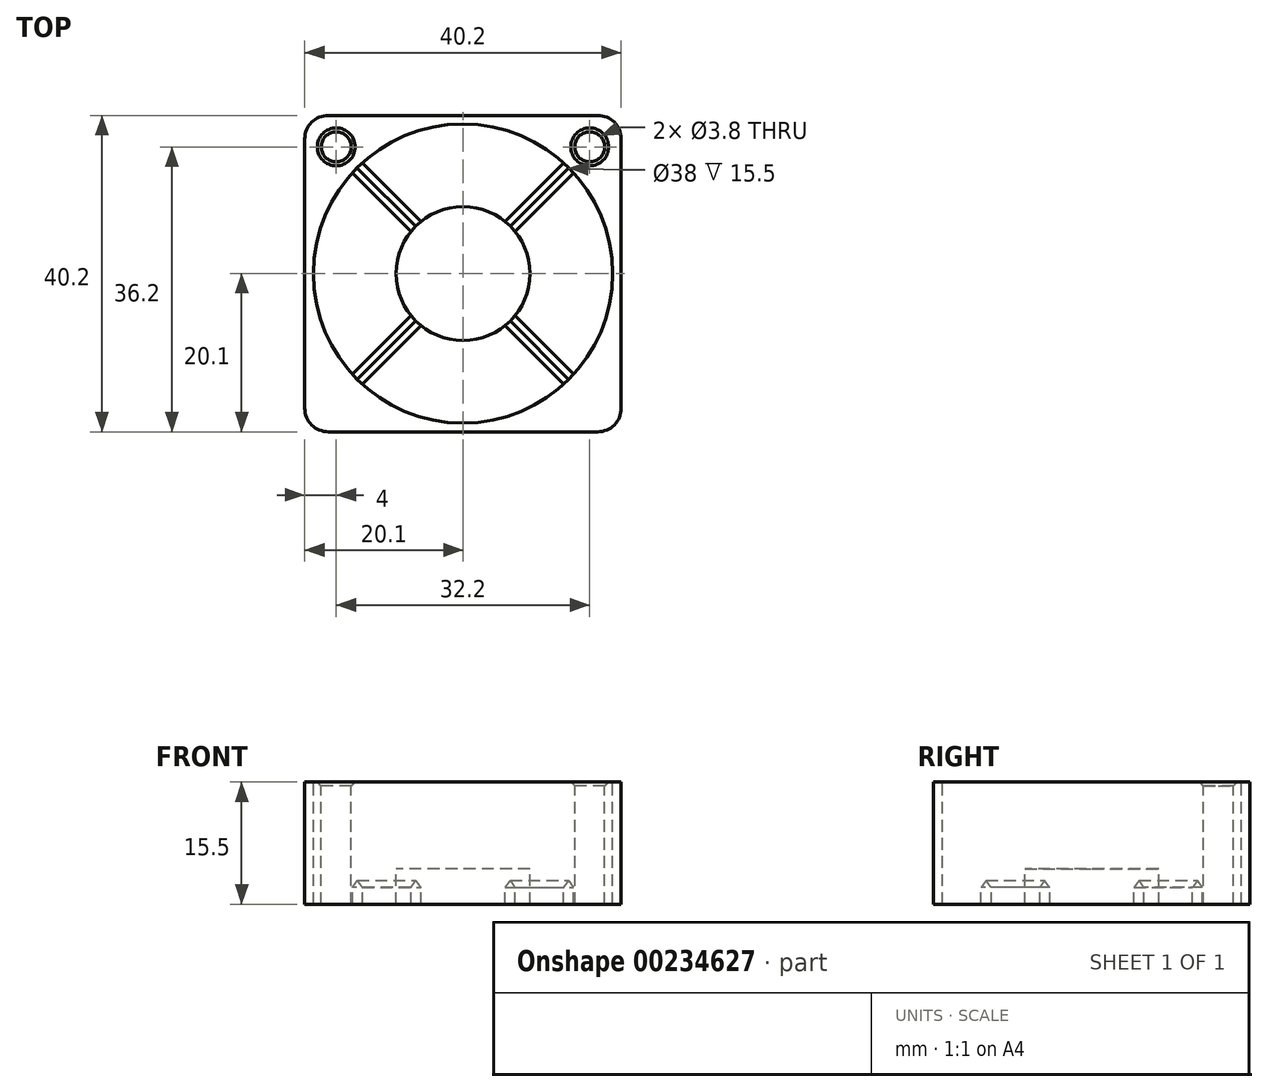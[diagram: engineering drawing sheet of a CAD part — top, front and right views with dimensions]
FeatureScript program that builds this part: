
annotation { "Feature Type Name" : "Feature", "Feature Type Description" : "" }
export const myFeature = defineFeature(function(context is Context, id is Id, definition is map)
    precondition{}
    {
        {
            var Q0;
            Q0=qCreatedBy(makeId("Top.planeOp"),FACE);
            var sketch = newSketch(context, id + "F0", { "sketchPlane" : qUnion([Q0])});
            skLineSegment(sketch, "E0.bottom", {"start": v(17.1, -20.1) * mm, "end": v(-17.1, -20.1) * mm});
            skLineSegment(sketch, "E0.top", {"start": v(17.1, 20.1) * mm, "end": v(-17.1, 20.1) * mm});
            skLineSegment(sketch, "E0.left", {"start": v(20.1, -17.1) * mm, "end": v(20.1, 17.1) * mm});
            skLineSegment(sketch, "E0.right", {"start": v(-20.1, -17.1) * mm, "end": v(-20.1, 17.1) * mm});
            skPoint(sketch, "E0.middle", {"position": v(0, 0) * mm});
            skPoint(sketch, "E1.visualSharp", {"position": v(-20.1, 20.1) * mm});
            skArc(sketch, "E1.filletArc", {"start": v(-17.1, 20.1) * mm, "mid": v(-19.22, 19.22) * mm, "end": v(-20.1, 17.1) * mm});
            skPoint(sketch, "E2.visualSharp", {"position": v(20.1, 20.1) * mm});
            skArc(sketch, "E2.filletArc", {"start": v(20.1, 17.1) * mm, "mid": v(19.22, 19.22) * mm, "end": v(17.1, 20.1) * mm});
            skPoint(sketch, "E3.visualSharp", {"position": v(20.1, -20.1) * mm});
            skArc(sketch, "E3.filletArc", {"start": v(17.1, -20.1) * mm, "mid": v(19.22, -19.22) * mm, "end": v(20.1, -17.1) * mm});
            skPoint(sketch, "E4.visualSharp", {"position": v(-20.1, -20.1) * mm});
            skArc(sketch, "E4.filletArc", {"start": v(-20.1, -17.1) * mm, "mid": v(-19.22, -19.22) * mm, "end": v(-17.1, -20.1) * mm});
            skCircle(sketch, "E5", {"center": v(0, 0) * mm, "radius": 19 * mm});
            skCircle(sketch, "E6", {"center": v(0, 0) * mm, "radius": 8.5 * mm});
            skLineSegment(sketch, "E7", {"start": v(-17.1, -17.1) * mm, "end": v(17.1, 17.1) * mm, "construction": true});
            skLineSegment(sketch, "E8", {"start": v(-17.1, 17.1) * mm, "end": v(17.1, -17.1) * mm, "construction": true});
            skLineSegment(sketch, "E9", {"start": v(-14.06, -12.78) * mm, "end": v(-6.61, -5.34) * mm});
            skLineSegment(sketch, "E10", {"start": v(-5.34, -6.61) * mm, "end": v(-12.78, -14.06) * mm});
            skLineSegment(sketch, "E11", {"start": v(12.78, -14.06) * mm, "end": v(5.34, -6.61) * mm});
            skLineSegment(sketch, "E12", {"start": v(6.61, -5.34) * mm, "end": v(14.06, -12.78) * mm});
            skLineSegment(sketch, "E13.MirrorCS", {"start": v(6.61, 5.34) * mm, "end": v(14.06, 12.78) * mm});
            skLineSegment(sketch, "E14.MirrorCS", {"start": v(12.78, 14.06) * mm, "end": v(5.34, 6.61) * mm});
            skLineSegment(sketch, "E15.MirrorCS", {"start": v(-5.34, 6.61) * mm, "end": v(-12.78, 14.06) * mm});
            skLineSegment(sketch, "E16.MirrorCS", {"start": v(-14.06, 12.78) * mm, "end": v(-6.61, 5.34) * mm});
            skCircle(sketch, "E17", {"center": v(-16.1, -16.1) * mm, "radius": 1.9 * mm});
            skCircle(sketch, "E18", {"center": v(16.1, -16.1) * mm, "radius": 1.9 * mm});
            skCircle(sketch, "E19.MirrorC", {"center": v(16.1, 16.1) * mm, "radius": 1.9 * mm});
            skCircle(sketch, "E20.MirrorC", {"center": v(-16.1, 16.1) * mm, "radius": 1.9 * mm});
            skLineSegment(sketch, "E21", {"start": v(20.1, 0) * mm, "end": v(-20.1, 0) * mm, "construction": true});
            skSolve(sketch);
        }
        {
            var Q0;
            Q0=makeQuery(id+"F0.imprint","IMPRINT",FACE,{"disambiguationData":[TD([[makeQuery(id+"F0.imprint","IMPRINT",EDGE,{"derivedFrom":sQuery(id+"F0.wireOp",EDGE,"E0.bottom")}),-1.0]])]});
            var Q1;
            {var subQ0=sQuery(id+"F0.wireOp",EDGE,"E15.MirrorCS");var subQ1=sQuery(id+"F0.wireOp",EDGE,"E5");var subQ2=makeQuery(id+"F0.imprint","INTERSECT",VERTEX,{"derivedFrom":[subQ1,subQ0]});Q1=makeQuery(id+"F0.imprint","IMPRINT",FACE,{"disambiguationData":[TD([[makeQuery(id+"F0.imprint","IMPRINT",EDGE,{"disambiguationData":[TD([[subQ2,-1.0]])],"derivedFrom":subQ1}),1.0]])]});}
            var Q2;
            {var subQ0=sQuery(id+"F0.wireOp",EDGE,"E15.MirrorCS");var subQ1=sQuery(id+"F0.wireOp",EDGE,"E6");var subQ2=makeQuery(id+"F0.imprint","INTERSECT",VERTEX,{"derivedFrom":[subQ1,subQ0]});Q2=makeQuery(id+"F0.imprint","IMPRINT",FACE,{"disambiguationData":[TD([[makeQuery(id+"F0.imprint","IMPRINT",EDGE,{"disambiguationData":[TD([[subQ2,-1.0]])],"derivedFrom":subQ1}),-1.0]])]});}
            var Q3;
            {var subQ0=sQuery(id+"F0.wireOp",EDGE,"OKVz19BP-hNnI-5fpd-Gdqc-Ac2bVMNZXSYf");var subQ1=sQuery(id+"F0.wireOp",EDGE,"E15.MirrorCS");var subQ2=makeQuery(id+"F0.imprint","INTERSECT",VERTEX,{"derivedFrom":[subQ1,subQ0]});Q3=makeQuery(id+"F0.imprint","IMPRINT",FACE,{"disambiguationData":[TD([[makeQuery(id+"F0.imprint","IMPRINT",EDGE,{"disambiguationData":[TD([[subQ2,-1.0]])],"derivedFrom":subQ1}),1.0]])]});}
            var Q4;
            {var subQ0=sQuery(id+"F0.wireOp",EDGE,"E13.MirrorCS");var subQ1=sQuery(id+"F0.wireOp",EDGE,"E5");var subQ2=makeQuery(id+"F0.imprint","INTERSECT",VERTEX,{"derivedFrom":[subQ1,subQ0]});Q4=makeQuery(id+"F0.imprint","IMPRINT",FACE,{"disambiguationData":[TD([[makeQuery(id+"F0.imprint","IMPRINT",EDGE,{"disambiguationData":[TD([[subQ2,-1.0]])],"derivedFrom":subQ1}),1.0]])]});}
            var Q5;
            {var subQ0=sQuery(id+"F0.wireOp",EDGE,"OKVz19BP-hNnI-5fpd-Gdqc-Ac2bVMNZXSYf");var subQ1=sQuery(id+"F0.wireOp",EDGE,"E13.MirrorCS");var subQ2=makeQuery(id+"F0.imprint","INTERSECT",VERTEX,{"derivedFrom":[subQ1,subQ0]});Q5=makeQuery(id+"F0.imprint","IMPRINT",FACE,{"disambiguationData":[TD([[makeQuery(id+"F0.imprint","IMPRINT",EDGE,{"disambiguationData":[TD([[subQ2,-1.0]])],"derivedFrom":subQ1}),1.0]])]});}
            var Q6;
            {var subQ0=sQuery(id+"F0.wireOp",EDGE,"E13.MirrorCS");var subQ1=sQuery(id+"F0.wireOp",EDGE,"E6");var subQ2=makeQuery(id+"F0.imprint","INTERSECT",VERTEX,{"derivedFrom":[subQ1,subQ0]});Q6=makeQuery(id+"F0.imprint","IMPRINT",FACE,{"disambiguationData":[TD([[makeQuery(id+"F0.imprint","IMPRINT",EDGE,{"disambiguationData":[TD([[subQ2,-1.0]])],"derivedFrom":subQ1}),-1.0]])]});}
            var Q7;
            {var subQ0=sQuery(id+"F0.wireOp",EDGE,"E6");var subQ5=makeQuery(id+"F0.imprint","INTERSECT",VERTEX,{"derivedFrom":[subQ0,sQuery(id+"F0.wireOp",EDGE,"E13.MirrorCS")]});Q7=makeQuery(id+"F0.imprint","IMPRINT",FACE,{"disambiguationData":[TD([[makeQuery(id+"F0.imprint","IMPRINT",EDGE,{"disambiguationData":[TD([[subQ5,-1.0]])],"derivedFrom":subQ0}),1.0]])]});}
            var Q8;
            {var subQ0=sQuery(id+"F0.wireOp",EDGE,"E11");var subQ1=sQuery(id+"F0.wireOp",EDGE,"E6");var subQ2=makeQuery(id+"F0.imprint","INTERSECT",VERTEX,{"derivedFrom":[subQ1,subQ0]});Q8=makeQuery(id+"F0.imprint","IMPRINT",FACE,{"disambiguationData":[TD([[makeQuery(id+"F0.imprint","IMPRINT",EDGE,{"disambiguationData":[TD([[subQ2,-1.0]])],"derivedFrom":subQ1}),-1.0]])]});}
            var Q9;
            {var subQ0=sQuery(id+"F0.wireOp",EDGE,"1LaAh6nE-W3w1-AZA4-EiVi-7yOxxJTW6hyr");var subQ1=sQuery(id+"F0.wireOp",EDGE,"E11");var subQ2=makeQuery(id+"F0.imprint","INTERSECT",VERTEX,{"derivedFrom":[subQ1,subQ0]});Q9=makeQuery(id+"F0.imprint","IMPRINT",FACE,{"disambiguationData":[TD([[makeQuery(id+"F0.imprint","IMPRINT",EDGE,{"disambiguationData":[TD([[subQ2,-1.0]])],"derivedFrom":subQ1}),-1.0]])]});}
            var Q10;
            {var subQ0=sQuery(id+"F0.wireOp",EDGE,"E11");var subQ1=sQuery(id+"F0.wireOp",EDGE,"E5");var subQ2=makeQuery(id+"F0.imprint","INTERSECT",VERTEX,{"derivedFrom":[subQ1,subQ0]});Q10=makeQuery(id+"F0.imprint","IMPRINT",FACE,{"disambiguationData":[TD([[makeQuery(id+"F0.imprint","IMPRINT",EDGE,{"disambiguationData":[TD([[subQ2,-1.0]])],"derivedFrom":subQ1}),1.0]])]});}
            var Q11;
            {var subQ0=sQuery(id+"F0.wireOp",EDGE,"1LaAh6nE-W3w1-AZA4-EiVi-7yOxxJTW6hyr");var subQ1=sQuery(id+"F0.wireOp",EDGE,"E9");var subQ2=makeQuery(id+"F0.imprint","INTERSECT",VERTEX,{"derivedFrom":[subQ1,subQ0]});Q11=makeQuery(id+"F0.imprint","IMPRINT",FACE,{"disambiguationData":[TD([[makeQuery(id+"F0.imprint","IMPRINT",EDGE,{"disambiguationData":[TD([[subQ2,-1.0]])],"derivedFrom":subQ1}),-1.0]])]});}
            var Q12;
            {var subQ0=sQuery(id+"F0.wireOp",EDGE,"E9");var subQ1=sQuery(id+"F0.wireOp",EDGE,"E6");var subQ2=makeQuery(id+"F0.imprint","INTERSECT",VERTEX,{"derivedFrom":[subQ1,subQ0]});Q12=makeQuery(id+"F0.imprint","IMPRINT",FACE,{"disambiguationData":[TD([[makeQuery(id+"F0.imprint","IMPRINT",EDGE,{"disambiguationData":[TD([[subQ2,-1.0]])],"derivedFrom":subQ1}),-1.0]])]});}
            var Q13;
            {var subQ0=sQuery(id+"F0.wireOp",EDGE,"E9");var subQ1=sQuery(id+"F0.wireOp",EDGE,"E5");var subQ2=makeQuery(id+"F0.imprint","INTERSECT",VERTEX,{"derivedFrom":[subQ1,subQ0]});Q13=makeQuery(id+"F0.imprint","IMPRINT",FACE,{"disambiguationData":[TD([[makeQuery(id+"F0.imprint","IMPRINT",EDGE,{"disambiguationData":[TD([[subQ2,-1.0]])],"derivedFrom":subQ1}),1.0]])]});}
            var Q14;
            Q14=makeQuery(id+"F0.imprint","IMPRINT",FACE,{"disambiguationData":[TD([[makeQuery(id+"F0.imprint","IMPRINT",EDGE,{"derivedFrom":sQuery(id+"F0.wireOp",EDGE,"E17")}),1.0]])]});
            var Q15;
            Q15=makeQuery(id+"F0.imprint","IMPRINT",FACE,{"disambiguationData":[TD([[makeQuery(id+"F0.imprint","IMPRINT",EDGE,{"derivedFrom":sQuery(id+"F0.wireOp",EDGE,"E18")}),1.0]])]});
            var Q16;
            Q16=makeQuery(id+"F0.imprint","IMPRINT",FACE,{"disambiguationData":[TD([[makeQuery(id+"F0.imprint","IMPRINT",EDGE,{"derivedFrom":sQuery(id+"F0.wireOp",EDGE,"E20.MirrorC")}),-1.0]])]});
            var Q17;
            Q17=makeQuery(id+"F0.imprint","IMPRINT",FACE,{"disambiguationData":[TD([[makeQuery(id+"F0.imprint","IMPRINT",EDGE,{"derivedFrom":sQuery(id+"F0.wireOp",EDGE,"E19.MirrorC")}),-1.0]])]});
            extrude(context, id + "F1", {"entities" : qUnion([Q0, Q1, Q2, Q3, Q4, Q5, Q6, Q7, Q8, Q9, Q10, Q11, Q12, Q13, Q14, Q15, Q16, Q17]), "oppositeDirection" : true, "depth" : 3 * mm});
        }
        {
            var Q0;
            Q0=makeQuery(id+"F0.imprint","IMPRINT",FACE,{"disambiguationData":[TD([[makeQuery(id+"F0.imprint","IMPRINT",EDGE,{"derivedFrom":sQuery(id+"F0.wireOp",EDGE,"E0.bottom")}),-1.0]])]});
            var Q1;
            {var subQ0=sQuery(id+"F0.wireOp",EDGE,"E6");var subQ5=makeQuery(id+"F0.imprint","INTERSECT",VERTEX,{"derivedFrom":[subQ0,sQuery(id+"F0.wireOp",EDGE,"E13.MirrorCS")]});Q1=makeQuery(id+"F0.imprint","IMPRINT",FACE,{"disambiguationData":[TD([[makeQuery(id+"F0.imprint","IMPRINT",EDGE,{"disambiguationData":[TD([[subQ5,-1.0]])],"derivedFrom":subQ0}),1.0]])]});}
            var Q2;
            Q2=makeQuery(id+"F0.imprint","IMPRINT",FACE,{"disambiguationData":[TD([[makeQuery(id+"F0.imprint","IMPRINT",EDGE,{"derivedFrom":sQuery(id+"F0.wireOp",EDGE,"E17")}),1.0]])]});
            var Q3;
            Q3=makeQuery(id+"F0.imprint","IMPRINT",FACE,{"disambiguationData":[TD([[makeQuery(id+"F0.imprint","IMPRINT",EDGE,{"derivedFrom":sQuery(id+"F0.wireOp",EDGE,"E18")}),1.0]])]});
            var Q4;
            Q4=makeQuery(id+"F0.imprint","IMPRINT",FACE,{"disambiguationData":[TD([[makeQuery(id+"F0.imprint","IMPRINT",EDGE,{"derivedFrom":sQuery(id+"F0.wireOp",EDGE,"E19.MirrorC")}),-1.0]])]});
            var Q5;
            Q5=makeQuery(id+"F0.imprint","IMPRINT",FACE,{"disambiguationData":[TD([[makeQuery(id+"F0.imprint","IMPRINT",EDGE,{"derivedFrom":sQuery(id+"F0.wireOp",EDGE,"E20.MirrorC")}),-1.0]])]});
            extrude(context, id + "F2", {"entities" : qUnion([Q0, Q1, Q2, Q3, Q4, Q5]), "operationType" : NewBodyOperationType.ADD, "depth" : 1.5 * mm});
        }
        {
            var Q0;
            Q0=makeQuery(id+"F0.imprint","IMPRINT",FACE,{"disambiguationData":[TD([[makeQuery(id+"F0.imprint","IMPRINT",EDGE,{"derivedFrom":sQuery(id+"F0.wireOp",EDGE,"E17")}),1.0]])]});
            var Q1;
            Q1=makeQuery(id+"F0.imprint","IMPRINT",FACE,{"disambiguationData":[TD([[makeQuery(id+"F0.imprint","IMPRINT",EDGE,{"derivedFrom":sQuery(id+"F0.wireOp",EDGE,"E18")}),1.0]])]});
            var Q2;
            Q2=makeQuery(id+"F0.imprint","IMPRINT",FACE,{"disambiguationData":[TD([[makeQuery(id+"F0.imprint","IMPRINT",EDGE,{"derivedFrom":sQuery(id+"F0.wireOp",EDGE,"E19.MirrorC")}),-1.0]])]});
            var Q3;
            Q3=makeQuery(id+"F0.imprint","IMPRINT",FACE,{"disambiguationData":[TD([[makeQuery(id+"F0.imprint","IMPRINT",EDGE,{"derivedFrom":sQuery(id+"F0.wireOp",EDGE,"E20.MirrorC")}),-1.0]])]});
            extrude(context, id + "F3", {"entities" : qUnion([Q0, Q1, Q2, Q3]), "operationType" : NewBodyOperationType.ADD, "depth" : 12.5 * mm});
        }
        {
            var Q0;
            Q0=makeQuery(id+"F2.opExtrude","CAP_EDGE",EDGE,{"disambiguationData":[OSD([sQuery(id+"F0.wireOp",EDGE,"E5")])],"isStart":false});
            var Q1;
            Q1=makeQuery(id+"F3.opExtrude","CAP_EDGE",EDGE,{"disambiguationData":[OSD([sQuery(id+"F0.wireOp",EDGE,"E18")])],"isStart":false});
            var Q2;
            Q2=makeQuery(id+"F3.opExtrude","CAP_EDGE",EDGE,{"disambiguationData":[OSD([sQuery(id+"F0.wireOp",EDGE,"E17")])],"isStart":false});
            var Q3;
            Q3=makeQuery(id+"F3.opExtrude","CAP_EDGE",EDGE,{"disambiguationData":[OSD([sQuery(id+"F0.wireOp",EDGE,"E20.MirrorC")])],"isStart":false});
            var Q4;
            Q4=makeQuery(id+"F3.opExtrude","CAP_EDGE",EDGE,{"disambiguationData":[OSD([sQuery(id+"F0.wireOp",EDGE,"E19.MirrorC")])],"isStart":false});
            chamfer(context, id + "F4", {"entities" : qUnion([Q0, Q1, Q2, Q3, Q4]), "width" : 0.5 * mm, "tangentPropagation" : true});
        }
        {
            var Q0;
            {var subQ0=sQuery(id+"F0.wireOp",EDGE,"OKVz19BP-hNnI-5fpd-Gdqc-Ac2bVMNZXSYf");Q0=makeQuery(id+"F1.opExtrude","CAP_EDGE",EDGE,{"disambiguationData":[OSD([subQ0]),TDD([makeQuery(id+"F0.imprint","IMPRINT",EDGE,{"disambiguationData":[TD([[makeQuery(id+"F0.imprint","INTERSECT",VERTEX,{"derivedFrom":[sQuery(id+"F0.wireOp",EDGE,"E10"),subQ0]}),-1.0]])],"derivedFrom":subQ0})])],"isStart":true});}
            var Q1;
            {var subQ0=sQuery(id+"F0.wireOp",EDGE,"1LaAh6nE-W3w1-AZA4-EiVi-7yOxxJTW6hyr");Q1=makeQuery(id+"F1.opExtrude","CAP_EDGE",EDGE,{"disambiguationData":[OSD([subQ0]),TDD([makeQuery(id+"F0.imprint","IMPRINT",EDGE,{"disambiguationData":[TD([[makeQuery(id+"F0.imprint","INTERSECT",VERTEX,{"derivedFrom":[sQuery(id+"F0.wireOp",EDGE,"E10"),subQ0]}),-1.0]])],"derivedFrom":subQ0})])],"isStart":true});}
            var Q2;
            {var subQ0=sQuery(id+"F0.wireOp",EDGE,"E11");Q2=makeQuery(id+"F1.opExtrude","CAP_EDGE",EDGE,{"disambiguationData":[OSD([subQ0]),TDD([makeQuery(id+"F0.imprint","IMPRINT",EDGE,{"disambiguationData":[TD([[makeQuery(id+"F0.imprint","INTERSECT",VERTEX,{"derivedFrom":[sQuery(id+"F0.wireOp",EDGE,"E5"),subQ0]}),-1.0]])],"derivedFrom":subQ0})])],"isStart":true});}
            var Q3;
            {var subQ0=sQuery(id+"F0.wireOp",EDGE,"E12");Q3=makeQuery(id+"F1.opExtrude","CAP_EDGE",EDGE,{"disambiguationData":[OSD([subQ0]),TDD([makeQuery(id+"F0.imprint","IMPRINT",EDGE,{"disambiguationData":[TD([[makeQuery(id+"F0.imprint","INTERSECT",VERTEX,{"derivedFrom":[sQuery(id+"F0.wireOp",EDGE,"E5"),subQ0]}),1.0]])],"derivedFrom":subQ0})])],"isStart":true});}
            var Q4;
            {var subQ0=sQuery(id+"F0.wireOp",EDGE,"E11");Q4=makeQuery(id+"F1.opExtrude","CAP_EDGE",EDGE,{"disambiguationData":[OSD([subQ0]),TDD([makeQuery(id+"F0.imprint","IMPRINT",EDGE,{"disambiguationData":[TD([[makeQuery(id+"F0.imprint","INTERSECT",VERTEX,{"derivedFrom":[sQuery(id+"F0.wireOp",EDGE,"E6"),subQ0]}),1.0]])],"derivedFrom":subQ0})])],"isStart":true});}
            var Q5;
            {var subQ0=sQuery(id+"F0.wireOp",EDGE,"E12");Q5=makeQuery(id+"F1.opExtrude","CAP_EDGE",EDGE,{"disambiguationData":[OSD([subQ0]),TDD([makeQuery(id+"F0.imprint","IMPRINT",EDGE,{"disambiguationData":[TD([[makeQuery(id+"F0.imprint","INTERSECT",VERTEX,{"derivedFrom":[sQuery(id+"F0.wireOp",EDGE,"E6"),subQ0]}),-1.0]])],"derivedFrom":subQ0})])],"isStart":true});}
            var Q6;
            {var subQ0=sQuery(id+"F0.wireOp",EDGE,"OKVz19BP-hNnI-5fpd-Gdqc-Ac2bVMNZXSYf");Q6=makeQuery(id+"F1.opExtrude","CAP_EDGE",EDGE,{"disambiguationData":[OSD([subQ0]),TDD([makeQuery(id+"F0.imprint","IMPRINT",EDGE,{"disambiguationData":[TD([[makeQuery(id+"F0.imprint","INTERSECT",VERTEX,{"derivedFrom":[sQuery(id+"F0.wireOp",EDGE,"E12"),subQ0]}),-1.0]])],"derivedFrom":subQ0})])],"isStart":true});}
            var Q7;
            {var subQ0=sQuery(id+"F0.wireOp",EDGE,"1LaAh6nE-W3w1-AZA4-EiVi-7yOxxJTW6hyr");Q7=makeQuery(id+"F1.opExtrude","CAP_EDGE",EDGE,{"disambiguationData":[OSD([subQ0]),TDD([makeQuery(id+"F0.imprint","IMPRINT",EDGE,{"disambiguationData":[TD([[makeQuery(id+"F0.imprint","INTERSECT",VERTEX,{"derivedFrom":[sQuery(id+"F0.wireOp",EDGE,"E12"),subQ0]}),-1.0]])],"derivedFrom":subQ0})])],"isStart":true});}
            var Q8;
            {var subQ0=sQuery(id+"F0.wireOp",EDGE,"E10");Q8=makeQuery(id+"F1.opExtrude","CAP_EDGE",EDGE,{"disambiguationData":[OSD([subQ0]),TDD([makeQuery(id+"F0.imprint","IMPRINT",EDGE,{"disambiguationData":[TD([[makeQuery(id+"F0.imprint","INTERSECT",VERTEX,{"derivedFrom":[sQuery(id+"F0.wireOp",EDGE,"E5"),subQ0]}),1.0]])],"derivedFrom":subQ0})])],"isStart":true});}
            var Q9;
            {var subQ0=sQuery(id+"F0.wireOp",EDGE,"E9");Q9=makeQuery(id+"F1.opExtrude","CAP_EDGE",EDGE,{"disambiguationData":[OSD([subQ0]),TDD([makeQuery(id+"F0.imprint","IMPRINT",EDGE,{"disambiguationData":[TD([[makeQuery(id+"F0.imprint","INTERSECT",VERTEX,{"derivedFrom":[sQuery(id+"F0.wireOp",EDGE,"E5"),subQ0]}),-1.0]])],"derivedFrom":subQ0})])],"isStart":true});}
            var Q10;
            {var subQ0=sQuery(id+"F0.wireOp",EDGE,"1LaAh6nE-W3w1-AZA4-EiVi-7yOxxJTW6hyr");Q10=makeQuery(id+"F1.opExtrude","CAP_EDGE",EDGE,{"disambiguationData":[OSD([subQ0]),TDD([makeQuery(id+"F0.imprint","IMPRINT",EDGE,{"disambiguationData":[TD([[makeQuery(id+"F0.imprint","INTERSECT",VERTEX,{"derivedFrom":[sQuery(id+"F0.wireOp",EDGE,"E9"),subQ0]}),1.0]])],"derivedFrom":subQ0})])],"isStart":true});}
            var Q11;
            {var subQ0=sQuery(id+"F0.wireOp",EDGE,"OKVz19BP-hNnI-5fpd-Gdqc-Ac2bVMNZXSYf");Q11=makeQuery(id+"F1.opExtrude","CAP_EDGE",EDGE,{"disambiguationData":[OSD([subQ0]),TDD([makeQuery(id+"F0.imprint","IMPRINT",EDGE,{"disambiguationData":[TD([[makeQuery(id+"F0.imprint","INTERSECT",VERTEX,{"derivedFrom":[sQuery(id+"F0.wireOp",EDGE,"E9"),subQ0]}),1.0]])],"derivedFrom":subQ0})])],"isStart":true});}
            var Q12;
            {var subQ0=sQuery(id+"F0.wireOp",EDGE,"E9");Q12=makeQuery(id+"F1.opExtrude","CAP_EDGE",EDGE,{"disambiguationData":[OSD([subQ0]),TDD([makeQuery(id+"F0.imprint","IMPRINT",EDGE,{"disambiguationData":[TD([[makeQuery(id+"F0.imprint","INTERSECT",VERTEX,{"derivedFrom":[sQuery(id+"F0.wireOp",EDGE,"E6"),subQ0]}),1.0]])],"derivedFrom":subQ0})])],"isStart":true});}
            var Q13;
            {var subQ0=sQuery(id+"F0.wireOp",EDGE,"E10");Q13=makeQuery(id+"F1.opExtrude","CAP_EDGE",EDGE,{"disambiguationData":[OSD([subQ0]),TDD([makeQuery(id+"F0.imprint","IMPRINT",EDGE,{"disambiguationData":[TD([[makeQuery(id+"F0.imprint","INTERSECT",VERTEX,{"derivedFrom":[sQuery(id+"F0.wireOp",EDGE,"E6"),subQ0]}),-1.0]])],"derivedFrom":subQ0})])],"isStart":true});}
            var Q14;
            {var subQ0=sQuery(id+"F0.wireOp",EDGE,"E16.MirrorCS");Q14=makeQuery(id+"F1.opExtrude","CAP_EDGE",EDGE,{"disambiguationData":[OSD([subQ0]),TDD([makeQuery(id+"F0.imprint","IMPRINT",EDGE,{"disambiguationData":[TD([[makeQuery(id+"F0.imprint","INTERSECT",VERTEX,{"derivedFrom":[sQuery(id+"F0.wireOp",EDGE,"E6"),subQ0]}),1.0]])],"derivedFrom":subQ0})])],"isStart":true});}
            var Q15;
            {var subQ0=sQuery(id+"F0.wireOp",EDGE,"E15.MirrorCS");Q15=makeQuery(id+"F1.opExtrude","CAP_EDGE",EDGE,{"disambiguationData":[OSD([subQ0]),TDD([makeQuery(id+"F0.imprint","IMPRINT",EDGE,{"disambiguationData":[TD([[makeQuery(id+"F0.imprint","INTERSECT",VERTEX,{"derivedFrom":[sQuery(id+"F0.wireOp",EDGE,"E6"),subQ0]}),-1.0]])],"derivedFrom":subQ0})])],"isStart":true});}
            var Q16;
            {var subQ0=sQuery(id+"F0.wireOp",EDGE,"OKVz19BP-hNnI-5fpd-Gdqc-Ac2bVMNZXSYf");Q16=makeQuery(id+"F1.opExtrude","CAP_EDGE",EDGE,{"disambiguationData":[OSD([subQ0]),TDD([makeQuery(id+"F0.imprint","IMPRINT",EDGE,{"disambiguationData":[TD([[makeQuery(id+"F0.imprint","INTERSECT",VERTEX,{"derivedFrom":[sQuery(id+"F0.wireOp",EDGE,"E14.MirrorCS"),subQ0]}),-1.0]])],"derivedFrom":subQ0})])],"isStart":true});}
            var Q17;
            {var subQ0=sQuery(id+"F0.wireOp",EDGE,"E14.MirrorCS");Q17=makeQuery(id+"F1.opExtrude","CAP_EDGE",EDGE,{"disambiguationData":[OSD([subQ0]),TDD([makeQuery(id+"F0.imprint","IMPRINT",EDGE,{"disambiguationData":[TD([[makeQuery(id+"F0.imprint","INTERSECT",VERTEX,{"derivedFrom":[sQuery(id+"F0.wireOp",EDGE,"E6"),subQ0]}),1.0]])],"derivedFrom":subQ0})])],"isStart":true});}
            var Q18;
            {var subQ0=sQuery(id+"F0.wireOp",EDGE,"E13.MirrorCS");Q18=makeQuery(id+"F1.opExtrude","CAP_EDGE",EDGE,{"disambiguationData":[OSD([subQ0]),TDD([makeQuery(id+"F0.imprint","IMPRINT",EDGE,{"disambiguationData":[TD([[makeQuery(id+"F0.imprint","INTERSECT",VERTEX,{"derivedFrom":[sQuery(id+"F0.wireOp",EDGE,"E6"),subQ0]}),-1.0]])],"derivedFrom":subQ0})])],"isStart":true});}
            var Q19;
            {var subQ0=sQuery(id+"F0.wireOp",EDGE,"E13.MirrorCS");Q19=makeQuery(id+"F1.opExtrude","CAP_EDGE",EDGE,{"disambiguationData":[OSD([subQ0]),TDD([makeQuery(id+"F0.imprint","IMPRINT",EDGE,{"disambiguationData":[TD([[makeQuery(id+"F0.imprint","INTERSECT",VERTEX,{"derivedFrom":[sQuery(id+"F0.wireOp",EDGE,"E5"),subQ0]}),1.0]])],"derivedFrom":subQ0})])],"isStart":true});}
            var Q20;
            {var subQ0=sQuery(id+"F0.wireOp",EDGE,"E14.MirrorCS");Q20=makeQuery(id+"F1.opExtrude","CAP_EDGE",EDGE,{"disambiguationData":[OSD([subQ0]),TDD([makeQuery(id+"F0.imprint","IMPRINT",EDGE,{"disambiguationData":[TD([[makeQuery(id+"F0.imprint","INTERSECT",VERTEX,{"derivedFrom":[sQuery(id+"F0.wireOp",EDGE,"E5"),subQ0]}),-1.0]])],"derivedFrom":subQ0})])],"isStart":true});}
            var Q21;
            {var subQ0=sQuery(id+"F0.wireOp",EDGE,"1LaAh6nE-W3w1-AZA4-EiVi-7yOxxJTW6hyr");Q21=makeQuery(id+"F1.opExtrude","CAP_EDGE",EDGE,{"disambiguationData":[OSD([subQ0]),TDD([makeQuery(id+"F0.imprint","IMPRINT",EDGE,{"disambiguationData":[TD([[makeQuery(id+"F0.imprint","INTERSECT",VERTEX,{"derivedFrom":[sQuery(id+"F0.wireOp",EDGE,"E14.MirrorCS"),subQ0]}),-1.0]])],"derivedFrom":subQ0})])],"isStart":true});}
            var Q22;
            {var subQ0=sQuery(id+"F0.wireOp",EDGE,"E16.MirrorCS");Q22=makeQuery(id+"F1.opExtrude","CAP_EDGE",EDGE,{"disambiguationData":[OSD([subQ0]),TDD([makeQuery(id+"F0.imprint","IMPRINT",EDGE,{"disambiguationData":[TD([[makeQuery(id+"F0.imprint","INTERSECT",VERTEX,{"derivedFrom":[sQuery(id+"F0.wireOp",EDGE,"E5"),subQ0]}),-1.0]])],"derivedFrom":subQ0})])],"isStart":true});}
            var Q23;
            {var subQ0=sQuery(id+"F0.wireOp",EDGE,"E15.MirrorCS");Q23=makeQuery(id+"F1.opExtrude","CAP_EDGE",EDGE,{"disambiguationData":[OSD([subQ0]),TDD([makeQuery(id+"F0.imprint","IMPRINT",EDGE,{"disambiguationData":[TD([[makeQuery(id+"F0.imprint","INTERSECT",VERTEX,{"derivedFrom":[sQuery(id+"F0.wireOp",EDGE,"E5"),subQ0]}),1.0]])],"derivedFrom":subQ0})])],"isStart":true});}
            chamfer(context, id + "F5", {"entities" : qUnion([Q0, Q1, Q2, Q3, Q4, Q5, Q6, Q7, Q8, Q9, Q10, Q11, Q12, Q13, Q14, Q15, Q16, Q17, Q18, Q19, Q20, Q21, Q22, Q23]), "width" : 0.9 * mm, "tangentPropagation" : true});
        }
    });
